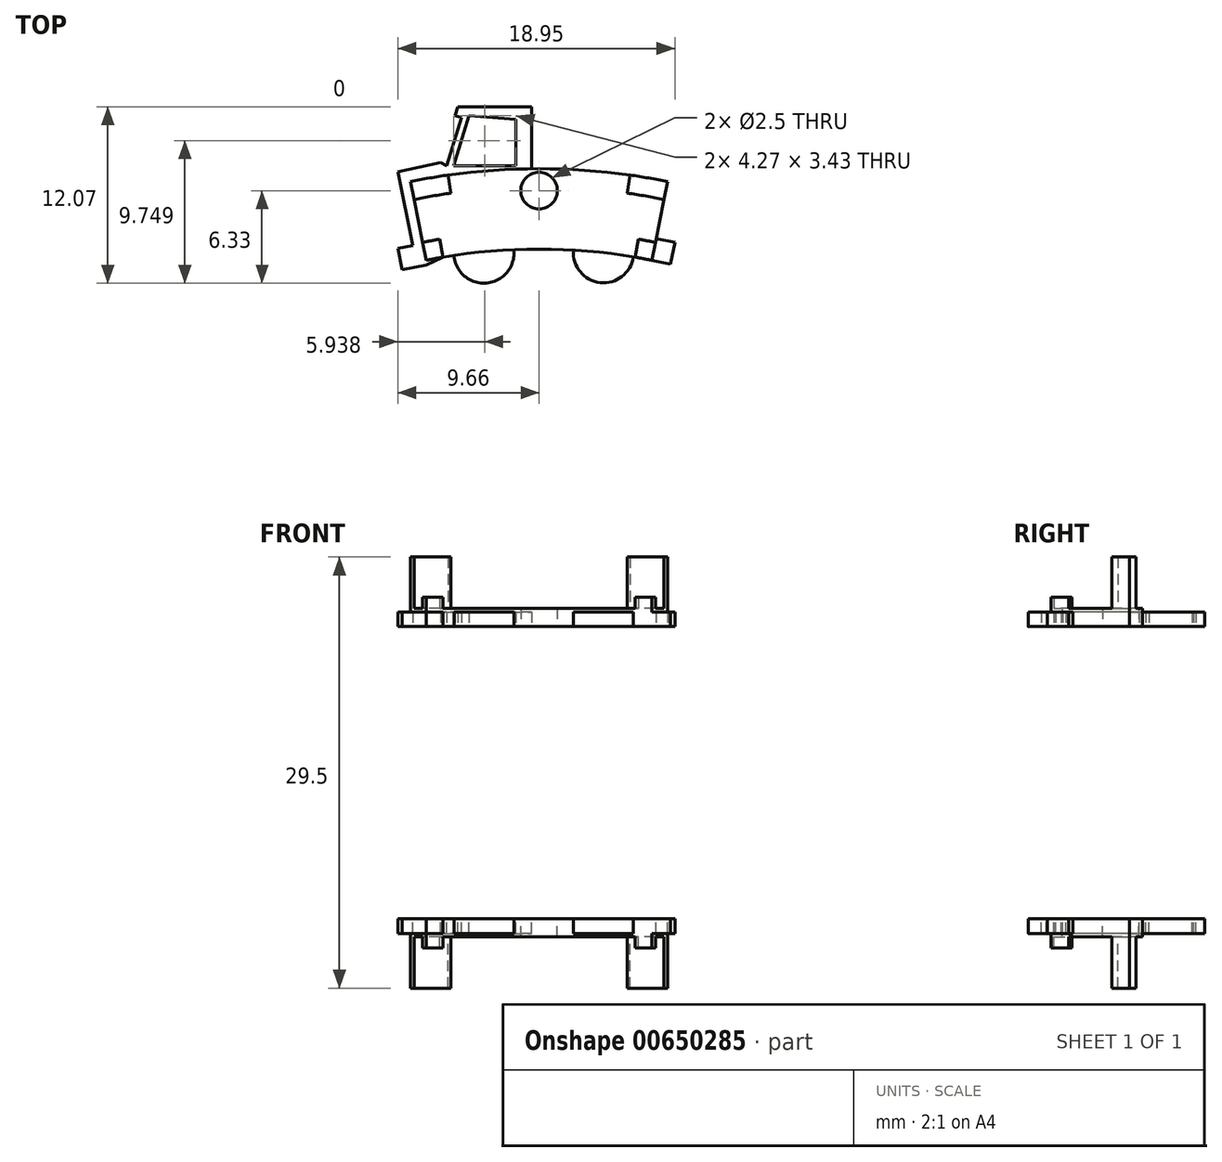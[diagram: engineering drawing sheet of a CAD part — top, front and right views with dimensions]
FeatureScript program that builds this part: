
annotation { "Feature Type Name" : "Feature", "Feature Type Description" : "" }
export const myFeature = defineFeature(function(context is Context, id is Id, definition is map)
    precondition{}
    {
        {
            var Q0;
            Q0=qCreatedBy(makeId("Top.planeOp"),FACE);
            var sketch = newSketch(context, id + "F0", { "sketchPlane" : qUnion([Q0])});
            skCircle(sketch, "E0", {"center": v(0, 0) * mm, "radius": 39 * mm});
            skCircle(sketch, "E1", {"center": v(0, 0) * mm, "radius": 44.5 * mm});
            skCircle(sketch, "E2", {"center": v(0, 43) * mm, "radius": 1.25 * mm});
            skCircle(sketch, "E3", {"center": v(0, 43) * mm, "radius": 6 * mm});
            skLineSegment(sketch, "E4", {"start": v(-7.7, 38.23) * mm, "end": v(-8.8, 43.62) * mm});
            skLineSegment(sketch, "E5", {"start": v(7.7, 38.23) * mm, "end": v(8.8, 43.62) * mm});
            skLineSegment(sketch, "E6", {"start": v(-7.5, 43.86) * mm, "end": v(-6.58, 38.44) * mm});
            skLineSegment(sketch, "E7", {"start": v(6.58, 38.44) * mm, "end": v(7.5, 43.86) * mm});
            skCircle(sketch, "E8", {"center": v(0, 0) * mm, "radius": 40.25 * mm});
            skCircle(sketch, "E9", {"center": v(0, 0) * mm, "radius": 43.25 * mm});
            skSolve(sketch);
        }
        {
            var Q0;
            {var subQ0=sQuery(id+"F0.wireOp",EDGE,"E7");var subQ1=sQuery(id+"F0.wireOp",EDGE,"E1");var subQ2=makeQuery(id+"F0.imprint","INTERSECT",VERTEX,{"derivedFrom":[subQ1,subQ0]});Q0=makeQuery(id+"F0.imprint","IMPRINT",FACE,{"disambiguationData":[TD([[makeQuery(id+"F0.imprint","IMPRINT",EDGE,{"disambiguationData":[TD([[subQ2,-1.0]])],"derivedFrom":subQ1}),1.0]])]});}
            var Q1;
            {var subQ0=sQuery(id+"F0.wireOp",EDGE,"E6");var subQ1=sQuery(id+"F0.wireOp",EDGE,"E1");var subQ2=makeQuery(id+"F0.imprint","INTERSECT",VERTEX,{"derivedFrom":[subQ1,subQ0]});Q1=makeQuery(id+"F0.imprint","IMPRINT",FACE,{"disambiguationData":[TD([[makeQuery(id+"F0.imprint","IMPRINT",EDGE,{"disambiguationData":[TD([[subQ2,1.0]])],"derivedFrom":subQ1}),1.0]])]});}
            var Q2;
            {var subQ0=sQuery(id+"F0.wireOp",EDGE,"E3");var subQ1=sQuery(id+"F0.wireOp",EDGE,"E1");var subQ2=makeQuery(id+"F0.imprint","INTERSECT",VERTEX,{"disambiguationData":[OD(0.0)],"derivedFrom":[subQ1,subQ0]});Q2=makeQuery(id+"F0.imprint","IMPRINT",FACE,{"disambiguationData":[TD([[makeQuery(id+"F0.imprint","IMPRINT",EDGE,{"disambiguationData":[TD([[subQ2,-1.0]])],"derivedFrom":subQ1}),1.0]])]});}
            var Q3;
            {var subQ0=sQuery(id+"F0.wireOp",EDGE,"E8");var subQ1=sQuery(id+"F0.wireOp",EDGE,"E3");var subQ2=makeQuery(id+"F0.imprint","INTERSECT",VERTEX,{"disambiguationData":[OD(1.0)],"derivedFrom":[subQ1,subQ0]});Q3=makeQuery(id+"F0.imprint","IMPRINT",FACE,{"disambiguationData":[TD([[makeQuery(id+"F0.imprint","IMPRINT",EDGE,{"disambiguationData":[TD([[subQ2,-1.0]])],"derivedFrom":subQ1}),-1.0]])]});}
            var Q4;
            {var subQ3=sQuery(id+"F0.wireOp",EDGE,"E9");var subQ5=sQuery(id+"F0.wireOp",EDGE,"E2");var subQ6=makeQuery(id+"F0.imprint","INTERSECT",VERTEX,{"disambiguationData":[OD(0.0)],"derivedFrom":[subQ5,subQ3]});Q4=makeQuery(id+"F0.imprint","IMPRINT",FACE,{"disambiguationData":[TD([[makeQuery(id+"F0.imprint","IMPRINT",EDGE,{"disambiguationData":[TD([[subQ6,1.0]])],"derivedFrom":subQ5}),-1.0]])]});}
            var Q5;
            {var subQ0=sQuery(id+"F0.wireOp",EDGE,"E9");var subQ1=sQuery(id+"F0.wireOp",EDGE,"E3");var subQ2=makeQuery(id+"F0.imprint","INTERSECT",VERTEX,{"disambiguationData":[OD(0.0)],"derivedFrom":[subQ1,subQ0]});Q5=makeQuery(id+"F0.imprint","IMPRINT",FACE,{"disambiguationData":[TD([[makeQuery(id+"F0.imprint","IMPRINT",EDGE,{"disambiguationData":[TD([[subQ2,-1.0]])],"derivedFrom":subQ1}),-1.0]])]});}
            var Q6;
            {var subQ0=sQuery(id+"F0.wireOp",EDGE,"E6");var subQ1=sQuery(id+"F0.wireOp",EDGE,"E0");var subQ2=makeQuery(id+"F0.imprint","INTERSECT",VERTEX,{"derivedFrom":[subQ1,subQ0]});Q6=makeQuery(id+"F0.imprint","IMPRINT",FACE,{"disambiguationData":[TD([[makeQuery(id+"F0.imprint","IMPRINT",EDGE,{"disambiguationData":[TD([[subQ2,1.0]])],"derivedFrom":subQ1}),-1.0]])]});}
            var Q7;
            {var subQ0=sQuery(id+"F0.wireOp",EDGE,"E3");var subQ1=sQuery(id+"F0.wireOp",EDGE,"E0");var subQ2=makeQuery(id+"F0.imprint","INTERSECT",VERTEX,{"disambiguationData":[OD(0.0)],"derivedFrom":[subQ1,subQ0]});Q7=makeQuery(id+"F0.imprint","IMPRINT",FACE,{"disambiguationData":[TD([[makeQuery(id+"F0.imprint","IMPRINT",EDGE,{"disambiguationData":[TD([[subQ2,-1.0]])],"derivedFrom":subQ1}),-1.0]])]});}
            var Q8;
            {var subQ0=sQuery(id+"F0.wireOp",EDGE,"E7");var subQ1=sQuery(id+"F0.wireOp",EDGE,"E0");var subQ2=makeQuery(id+"F0.imprint","INTERSECT",VERTEX,{"derivedFrom":[subQ1,subQ0]});Q8=makeQuery(id+"F0.imprint","IMPRINT",FACE,{"disambiguationData":[TD([[makeQuery(id+"F0.imprint","IMPRINT",EDGE,{"disambiguationData":[TD([[subQ2,-1.0]])],"derivedFrom":subQ1}),-1.0]])]});}
            var Q9;
            {var subQ0=sQuery(id+"F0.wireOp",EDGE,"E8");var subQ1=sQuery(id+"F0.wireOp",EDGE,"E5");var subQ2=makeQuery(id+"F0.imprint","INTERSECT",VERTEX,{"derivedFrom":[subQ1,subQ0]});Q9=makeQuery(id+"F0.imprint","IMPRINT",FACE,{"disambiguationData":[TD([[makeQuery(id+"F0.imprint","IMPRINT",EDGE,{"disambiguationData":[TD([[subQ2,-1.0]])],"derivedFrom":subQ1}),1.0]])]});}
            var Q10;
            {var subQ0=sQuery(id+"F0.wireOp",EDGE,"E8");var subQ1=sQuery(id+"F0.wireOp",EDGE,"E4");var subQ2=makeQuery(id+"F0.imprint","INTERSECT",VERTEX,{"derivedFrom":[subQ1,subQ0]});Q10=makeQuery(id+"F0.imprint","IMPRINT",FACE,{"disambiguationData":[TD([[makeQuery(id+"F0.imprint","IMPRINT",EDGE,{"disambiguationData":[TD([[subQ2,-1.0]])],"derivedFrom":subQ1}),-1.0]])]});}
            extrude(context, id + "F1", {"entities" : qUnion([Q0, Q1, Q2, Q3, Q4, Q5, Q6, Q7, Q8, Q9, Q10]), "depth" : 1.25 * mm, "offsetDistance" : 25 * mm});
        }
        {
            var Q0;
            Q0=qCreatedBy(makeId("Top.planeOp"),FACE);
            var sketch = newSketch(context, id + "F2", { "sketchPlane" : qUnion([Q0])});
            skCircle(sketch, "E10", {"center": v(0, 0) * mm, "radius": 39 * mm});
            skCircle(sketch, "E11", {"center": v(0, 0) * mm, "radius": 44.5 * mm});
            skCircle(sketch, "E12", {"center": v(0, 43) * mm, "radius": 0.85 * mm});
            skCircle(sketch, "E13", {"center": v(0, 43) * mm, "radius": 6 * mm});
            skLineSegment(sketch, "E14", {"start": v(-7.7, 38.23) * mm, "end": v(-8.8, 43.62) * mm});
            skLineSegment(sketch, "E15", {"start": v(7.7, 38.23) * mm, "end": v(8.8, 43.62) * mm});
            skLineSegment(sketch, "E16", {"start": v(-6.2, 44.06) * mm, "end": v(-5.44, 38.62) * mm});
            skLineSegment(sketch, "E17", {"start": v(5.44, 38.62) * mm, "end": v(6.2, 44.06) * mm});
            skCircle(sketch, "E18", {"center": v(0, 0) * mm, "radius": 40.25 * mm});
            skCircle(sketch, "E19", {"center": v(0, 0) * mm, "radius": 43.25 * mm});
            skSolve(sketch);
        }
        {
            var Q0;
            {var subQ0=sQuery(id+"F2.wireOp",EDGE,"E15");var subQ1=sQuery(id+"F2.wireOp",EDGE,"E11");var subQ2=makeQuery(id+"F2.imprint","INTERSECT",VERTEX,{"derivedFrom":[subQ1,subQ0]});Q0=makeQuery(id+"F2.imprint","IMPRINT",FACE,{"disambiguationData":[TD([[makeQuery(id+"F2.imprint","IMPRINT",EDGE,{"disambiguationData":[TD([[subQ2,-1.0]])],"derivedFrom":subQ1}),1.0]])]});}
            var Q1;
            {var subQ0=sQuery(id+"F2.wireOp",EDGE,"E14");var subQ1=sQuery(id+"F2.wireOp",EDGE,"E11");var subQ2=makeQuery(id+"F2.imprint","INTERSECT",VERTEX,{"derivedFrom":[subQ1,subQ0]});Q1=makeQuery(id+"F2.imprint","IMPRINT",FACE,{"disambiguationData":[TD([[makeQuery(id+"F2.imprint","IMPRINT",EDGE,{"disambiguationData":[TD([[subQ2,1.0]])],"derivedFrom":subQ1}),1.0]])]});}
            extrude(context, id + "F3", {"entities" : qUnion([Q0, Q1]), "operationType" : NewBodyOperationType.ADD, "depth" : 4.75 * mm, "offsetDistance" : 25 * mm});
        }
        {
            var Q0;
            Q0=qCreatedBy(makeId("Top.planeOp"),FACE);
            var sketch = newSketch(context, id + "F4", { "sketchPlane" : qUnion([Q0])});
            skCircle(sketch, "E20", {"center": v(0, 0) * mm, "radius": 39 * mm});
            skCircle(sketch, "E21", {"center": v(0, 0) * mm, "radius": 44.5 * mm});
            skCircle(sketch, "E22", {"center": v(0, 43) * mm, "radius": 0.85 * mm});
            skCircle(sketch, "E23", {"center": v(0, 43) * mm, "radius": 6 * mm});
            skLineSegment(sketch, "E24", {"start": v(-7.7, 38.23) * mm, "end": v(-8.8, 43.62) * mm});
            skLineSegment(sketch, "E25", {"start": v(7.7, 38.23) * mm, "end": v(8.8, 43.62) * mm});
            skLineSegment(sketch, "E26", {"start": v(-7.5, 43.86) * mm, "end": v(-6.58, 38.44) * mm});
            skLineSegment(sketch, "E27", {"start": v(6.58, 38.44) * mm, "end": v(7.5, 43.86) * mm});
            skCircle(sketch, "E28", {"center": v(0, 0) * mm, "radius": 40.25 * mm});
            skCircle(sketch, "E29", {"center": v(0, 0) * mm, "radius": 43.25 * mm});
            skSolve(sketch);
        }
        {
            var Q0;
            {var subQ0=sQuery(id+"F4.wireOp",EDGE,"E24");var subQ1=sQuery(id+"F4.wireOp",EDGE,"E20");var subQ2=makeQuery(id+"F4.imprint","INTERSECT",VERTEX,{"derivedFrom":[subQ1,subQ0]});Q0=makeQuery(id+"F4.imprint","IMPRINT",FACE,{"disambiguationData":[TD([[makeQuery(id+"F4.imprint","IMPRINT",EDGE,{"disambiguationData":[TD([[subQ2,1.0]])],"derivedFrom":subQ1}),-1.0]])]});}
            var Q1;
            {var subQ0=sQuery(id+"F4.wireOp",EDGE,"E25");var subQ1=sQuery(id+"F4.wireOp",EDGE,"E20");var subQ2=makeQuery(id+"F4.imprint","INTERSECT",VERTEX,{"derivedFrom":[subQ1,subQ0]});Q1=makeQuery(id+"F4.imprint","IMPRINT",FACE,{"disambiguationData":[TD([[makeQuery(id+"F4.imprint","IMPRINT",EDGE,{"disambiguationData":[TD([[subQ2,-1.0]])],"derivedFrom":subQ1}),-1.0]])]});}
            extrude(context, id + "F5", {"entities" : qUnion([Q0, Q1]), "operationType" : NewBodyOperationType.ADD, "depth" : 2 * mm, "offsetDistance" : 25 * mm});
        }
        {
            var Q0;
            {var subQ0=sQuery(id+"F4.wireOp",EDGE,"E28");var subQ1=sQuery(id+"F4.wireOp",EDGE,"E20");var subQ2=sQuery(id+"F2.wireOp",EDGE,"E19");var subQ3=sQuery(id+"F2.wireOp",EDGE,"E11");Q0=makeQuery(id+"F5.boolean.opBoolean","MERGE",FACE,{"derivedFrom":[makeQuery(id+"F3.boolean.opBoolean","MERGE",FACE,{"derivedFrom":[makeQuery(id+"F1.opExtrude","CAP_FACE",FACE,{"disambiguationData":[OSD([sQuery(id+"F0.wireOp",EDGE,"E0"),sQuery(id+"F0.wireOp",EDGE,"E1"),sQuery(id+"F0.wireOp",EDGE,"E2"),sQuery(id+"F0.wireOp",EDGE,"E4"),sQuery(id+"F0.wireOp",EDGE,"E5"),sQuery(id+"F0.wireOp",EDGE,"E6"),sQuery(id+"F0.wireOp",EDGE,"E7"),sQuery(id+"F0.wireOp",EDGE,"E8"),sQuery(id+"F0.wireOp",EDGE,"E9")])],"isStart":true}),makeQuery(id+"F3.opExtrude","CAP_FACE",FACE,{"disambiguationData":[OSD([subQ3,sQuery(id+"F2.wireOp",EDGE,"E15"),sQuery(id+"F2.wireOp",EDGE,"E17"),subQ2])],"isStart":true}),makeQuery(id+"F3.opExtrude","CAP_FACE",FACE,{"disambiguationData":[OSD([subQ3,sQuery(id+"F2.wireOp",EDGE,"E14"),sQuery(id+"F2.wireOp",EDGE,"E16"),subQ2])],"isStart":true})]}),makeQuery(id+"F5.opExtrude","CAP_FACE",FACE,{"disambiguationData":[OSD([subQ1,sQuery(id+"F4.wireOp",EDGE,"E25"),sQuery(id+"F4.wireOp",EDGE,"E27"),subQ0])],"isStart":true}),makeQuery(id+"F5.opExtrude","CAP_FACE",FACE,{"disambiguationData":[OSD([subQ1,sQuery(id+"F4.wireOp",EDGE,"E24"),sQuery(id+"F4.wireOp",EDGE,"E26"),subQ0])],"isStart":true})]});}
            var sketch = newSketch(context, id + "F6", { "sketchPlane" : qUnion([Q0])});
            skLineSegment(sketch, "E30", {"start": v(-0.52, -44.5) * mm, "end": v(-0.52, -48.74) * mm});
            skLineSegment(sketch, "E31", {"start": v(-0.52, -48.74) * mm, "end": v(-5.56, -48.74) * mm});
            skLineSegment(sketch, "E32", {"start": v(-5.56, -48.74) * mm, "end": v(-6.72, -44.94) * mm});
            skLineSegment(sketch, "E33", {"start": v(-6.72, -44.94) * mm, "end": v(-9.66, -44.28) * mm});
            skLineSegment(sketch, "E34", {"start": v(-9.66, -44.28) * mm, "end": v(-8.64, -39.25) * mm});
            skLineSegment(sketch, "E35", {"start": v(-8.64, -39.25) * mm, "end": v(-9.66, -39.04) * mm});
            skLineSegment(sketch, "E36", {"start": v(-9.66, -39.04) * mm, "end": v(-9.36, -37.58) * mm});
            skLineSegment(sketch, "E37", {"start": v(-9.36, -37.58) * mm, "end": v(-7.7, -37.9) * mm});
            skLineSegment(sketch, "E38", {"start": v(-7.7, -37.9) * mm, "end": v(-6.57, -38.44) * mm});
            skLineSegment(sketch, "E39", {"start": v(-6.57, -38.44) * mm, "end": v(-0.52, -44.5) * mm});
            skSolve(sketch);
        }
        {
            var Q0;
            Q0 = qSketchRegion(id + "F6", true);
            extrude(context, id + "F7", {"entities" : qUnion([Q0]), "operationType" : NewBodyOperationType.ADD, "oppositeDirection" : true, "depth" : 1 * mm, "offsetDistance" : 25 * mm});
        }
        {
            var Q0;
            {var subQ0=sQuery(id+"F4.wireOp",EDGE,"E28");var subQ1=sQuery(id+"F4.wireOp",EDGE,"E20");var subQ2=sQuery(id+"F2.wireOp",EDGE,"E19");var subQ3=sQuery(id+"F2.wireOp",EDGE,"E11");Q0=makeQuery(id+"F7.boolean.opBoolean","MERGE",FACE,{"derivedFrom":[makeQuery(id+"F5.boolean.opBoolean","MERGE",FACE,{"derivedFrom":[makeQuery(id+"F3.boolean.opBoolean","MERGE",FACE,{"derivedFrom":[makeQuery(id+"F1.opExtrude","CAP_FACE",FACE,{"disambiguationData":[OSD([sQuery(id+"F0.wireOp",EDGE,"E0"),sQuery(id+"F0.wireOp",EDGE,"E1"),sQuery(id+"F0.wireOp",EDGE,"E2"),sQuery(id+"F0.wireOp",EDGE,"E4"),sQuery(id+"F0.wireOp",EDGE,"E5"),sQuery(id+"F0.wireOp",EDGE,"E6"),sQuery(id+"F0.wireOp",EDGE,"E7"),sQuery(id+"F0.wireOp",EDGE,"E8"),sQuery(id+"F0.wireOp",EDGE,"E9")])],"isStart":true}),makeQuery(id+"F3.opExtrude","CAP_FACE",FACE,{"disambiguationData":[OSD([subQ3,sQuery(id+"F2.wireOp",EDGE,"E15"),sQuery(id+"F2.wireOp",EDGE,"E17"),subQ2])],"isStart":true}),makeQuery(id+"F3.opExtrude","CAP_FACE",FACE,{"disambiguationData":[OSD([subQ3,sQuery(id+"F2.wireOp",EDGE,"E14"),sQuery(id+"F2.wireOp",EDGE,"E16"),subQ2])],"isStart":true})]}),makeQuery(id+"F5.opExtrude","CAP_FACE",FACE,{"disambiguationData":[OSD([subQ1,sQuery(id+"F4.wireOp",EDGE,"E25"),sQuery(id+"F4.wireOp",EDGE,"E27"),subQ0])],"isStart":true}),makeQuery(id+"F5.opExtrude","CAP_FACE",FACE,{"disambiguationData":[OSD([subQ1,sQuery(id+"F4.wireOp",EDGE,"E24"),sQuery(id+"F4.wireOp",EDGE,"E26"),subQ0])],"isStart":true})]}),makeQuery(id+"F7.opExtrude","CAP_FACE",FACE,{"disambiguationData":[OSD([sQuery(id+"F6.wireOp",EDGE,"E30"),sQuery(id+"F6.wireOp",EDGE,"E31"),sQuery(id+"F6.wireOp",EDGE,"E32"),sQuery(id+"F6.wireOp",EDGE,"E33"),sQuery(id+"F6.wireOp",EDGE,"E34"),sQuery(id+"F6.wireOp",EDGE,"E35"),sQuery(id+"F6.wireOp",EDGE,"E36"),sQuery(id+"F6.wireOp",EDGE,"E37"),sQuery(id+"F6.wireOp",EDGE,"E38"),sQuery(id+"F6.wireOp",EDGE,"E39")])],"isStart":true})]});}
            var sketch = newSketch(context, id + "F8", { "sketchPlane" : qUnion([Q0])});
            skCircle(sketch, "E40", {"center": v(4.4, -38.75) * mm, "radius": 2.06 * mm});
            skCircle(sketch, "E41", {"center": v(-3.77, -38.73) * mm, "radius": 2.06 * mm});
            skLineSegment(sketch, "E42", {"start": v(7.7, -38.23) * mm, "end": v(9, -37.97) * mm});
            skLineSegment(sketch, "E43", {"start": v(9, -37.97) * mm, "end": v(9.3, -39.46) * mm});
            skLineSegment(sketch, "E44", {"start": v(9.3, -39.46) * mm, "end": v(8, -39.72) * mm});
            skLineSegment(sketch, "E45", {"start": v(8, -39.72) * mm, "end": v(7.7, -38.23) * mm});
            skSolve(sketch);
        }
        {
            var Q0;
            Q0 = qSketchRegion(id + "F8", true);
            extrude(context, id + "F9", {"entities" : qUnion([Q0]), "operationType" : NewBodyOperationType.ADD, "oppositeDirection" : true, "depth" : 1 * mm, "offsetDistance" : 25 * mm});
        }
        {
            var Q0;
            {var subQ0=sQuery(id+"F4.wireOp",EDGE,"E28");var subQ1=sQuery(id+"F4.wireOp",EDGE,"E20");var subQ2=sQuery(id+"F2.wireOp",EDGE,"E19");var subQ3=sQuery(id+"F2.wireOp",EDGE,"E11");Q0=makeQuery(id+"F9.boolean.opBoolean","MERGE",FACE,{"derivedFrom":[makeQuery(id+"F7.boolean.opBoolean","MERGE",FACE,{"derivedFrom":[makeQuery(id+"F5.boolean.opBoolean","MERGE",FACE,{"derivedFrom":[makeQuery(id+"F3.boolean.opBoolean","MERGE",FACE,{"derivedFrom":[makeQuery(id+"F1.opExtrude","CAP_FACE",FACE,{"disambiguationData":[OSD([sQuery(id+"F0.wireOp",EDGE,"E0"),sQuery(id+"F0.wireOp",EDGE,"E1"),sQuery(id+"F0.wireOp",EDGE,"E2"),sQuery(id+"F0.wireOp",EDGE,"E4"),sQuery(id+"F0.wireOp",EDGE,"E5"),sQuery(id+"F0.wireOp",EDGE,"E6"),sQuery(id+"F0.wireOp",EDGE,"E7"),sQuery(id+"F0.wireOp",EDGE,"E8"),sQuery(id+"F0.wireOp",EDGE,"E9")])],"isStart":true}),makeQuery(id+"F3.opExtrude","CAP_FACE",FACE,{"disambiguationData":[OSD([subQ3,sQuery(id+"F2.wireOp",EDGE,"E15"),sQuery(id+"F2.wireOp",EDGE,"E17"),subQ2])],"isStart":true}),makeQuery(id+"F3.opExtrude","CAP_FACE",FACE,{"disambiguationData":[OSD([subQ3,sQuery(id+"F2.wireOp",EDGE,"E14"),sQuery(id+"F2.wireOp",EDGE,"E16"),subQ2])],"isStart":true})]}),makeQuery(id+"F5.opExtrude","CAP_FACE",FACE,{"disambiguationData":[OSD([subQ1,sQuery(id+"F4.wireOp",EDGE,"E25"),sQuery(id+"F4.wireOp",EDGE,"E27"),subQ0])],"isStart":true}),makeQuery(id+"F5.opExtrude","CAP_FACE",FACE,{"disambiguationData":[OSD([subQ1,sQuery(id+"F4.wireOp",EDGE,"E24"),sQuery(id+"F4.wireOp",EDGE,"E26"),subQ0])],"isStart":true})]}),makeQuery(id+"F7.opExtrude","CAP_FACE",FACE,{"disambiguationData":[OSD([sQuery(id+"F6.wireOp",EDGE,"E30"),sQuery(id+"F6.wireOp",EDGE,"E31"),sQuery(id+"F6.wireOp",EDGE,"E32"),sQuery(id+"F6.wireOp",EDGE,"E33"),sQuery(id+"F6.wireOp",EDGE,"E34"),sQuery(id+"F6.wireOp",EDGE,"E35"),sQuery(id+"F6.wireOp",EDGE,"E36"),sQuery(id+"F6.wireOp",EDGE,"E37"),sQuery(id+"F6.wireOp",EDGE,"E38"),sQuery(id+"F6.wireOp",EDGE,"E39")])],"isStart":true})]}),makeQuery(id+"F9.opExtrude","CAP_FACE",FACE,{"disambiguationData":[OSD([sQuery(id+"F8.wireOp",EDGE,"E40")])],"isStart":true}),makeQuery(id+"F9.opExtrude","CAP_FACE",FACE,{"disambiguationData":[OSD([sQuery(id+"F8.wireOp",EDGE,"E41")])],"isStart":true}),makeQuery(id+"F9.opExtrude","CAP_FACE",FACE,{"disambiguationData":[OSD([sQuery(id+"F8.wireOp",EDGE,"E42"),sQuery(id+"F8.wireOp",EDGE,"E43"),sQuery(id+"F8.wireOp",EDGE,"E44"),sQuery(id+"F8.wireOp",EDGE,"E45")])],"isStart":true})]});}
            var sketch = newSketch(context, id + "F10", { "sketchPlane" : qUnion([Q0])});
            skLineSegment(sketch, "E46", {"start": v(-1.59, -47.88) * mm, "end": v(-1.59, -44.7) * mm});
            skLineSegment(sketch, "E47", {"start": v(-1.59, -44.7) * mm, "end": v(-5.86, -44.7) * mm});
            skLineSegment(sketch, "E48", {"start": v(-5.86, -44.7) * mm, "end": v(-4.8, -48.13) * mm});
            skLineSegment(sketch, "E49", {"start": v(-4.8, -48.13) * mm, "end": v(-1.59, -47.88) * mm});
            skLineSegment(sketch, "E50", {"start": v(-5.74, -48.13) * mm, "end": v(-5.31, -48) * mm});
            skLineSegment(sketch, "E51", {"start": v(-5.31, -48) * mm, "end": v(-6.32, -44.7) * mm});
            skLineSegment(sketch, "E52", {"start": v(-6.32, -44.7) * mm, "end": v(-7.88, -45.54) * mm});
            skLineSegment(sketch, "E53", {"start": v(-7.88, -45.54) * mm, "end": v(-6.33, -48.43) * mm});
            skLineSegment(sketch, "E54", {"start": v(-6.33, -48.43) * mm, "end": v(-5.74, -48.13) * mm});
            skSolve(sketch);
        }
        {
            var Q0;
            Q0 = qSketchRegion(id + "F10", true);
            extrude(context, id + "F11", {"entities" : qUnion([Q0]), "operationType" : NewBodyOperationType.REMOVE, "oppositeDirection" : true, "depth" : 25 * mm, "offsetDistance" : 25 * mm});
        }
        {
            var Q0;
            Q0=makeQuery(id+"F1.opExtrude","SWEPT_BODY",BODY,{"disambiguationData":[OSD([sQuery(id+"F0.wireOp",EDGE,"E0"),sQuery(id+"F0.wireOp",EDGE,"E1"),sQuery(id+"F0.wireOp",EDGE,"E2"),sQuery(id+"F0.wireOp",EDGE,"E4"),sQuery(id+"F0.wireOp",EDGE,"E5"),sQuery(id+"F0.wireOp",EDGE,"E6"),sQuery(id+"F0.wireOp",EDGE,"E7"),sQuery(id+"F0.wireOp",EDGE,"E8"),sQuery(id+"F0.wireOp",EDGE,"E9")])]});
            transform(context, id + "F12", {"entities" : qUnion([Q0]), "transformType" : TransformType.TRANSLATION_3D, "dx" : 0 * mm, "dy" : 0 * mm, "dz" : 10 * mm, "makeCopy" : false});
        }
        {
            var Q0;
            Q0=makeQuery(id+"F1.opExtrude","SWEPT_BODY",BODY,{"disambiguationData":[OSD([sQuery(id+"F0.wireOp",EDGE,"E0"),sQuery(id+"F0.wireOp",EDGE,"E1"),sQuery(id+"F0.wireOp",EDGE,"E2"),sQuery(id+"F0.wireOp",EDGE,"E4"),sQuery(id+"F0.wireOp",EDGE,"E5"),sQuery(id+"F0.wireOp",EDGE,"E6"),sQuery(id+"F0.wireOp",EDGE,"E7"),sQuery(id+"F0.wireOp",EDGE,"E8"),sQuery(id+"F0.wireOp",EDGE,"E9")])]});
            var Q1;
            Q1=qCreatedBy(makeId("Top.planeOp"),FACE);
            mirror(context, id + "F13", {"entities" : qUnion([Q0]), "mirrorPlane" : qUnion([Q1])});
        }
    });
